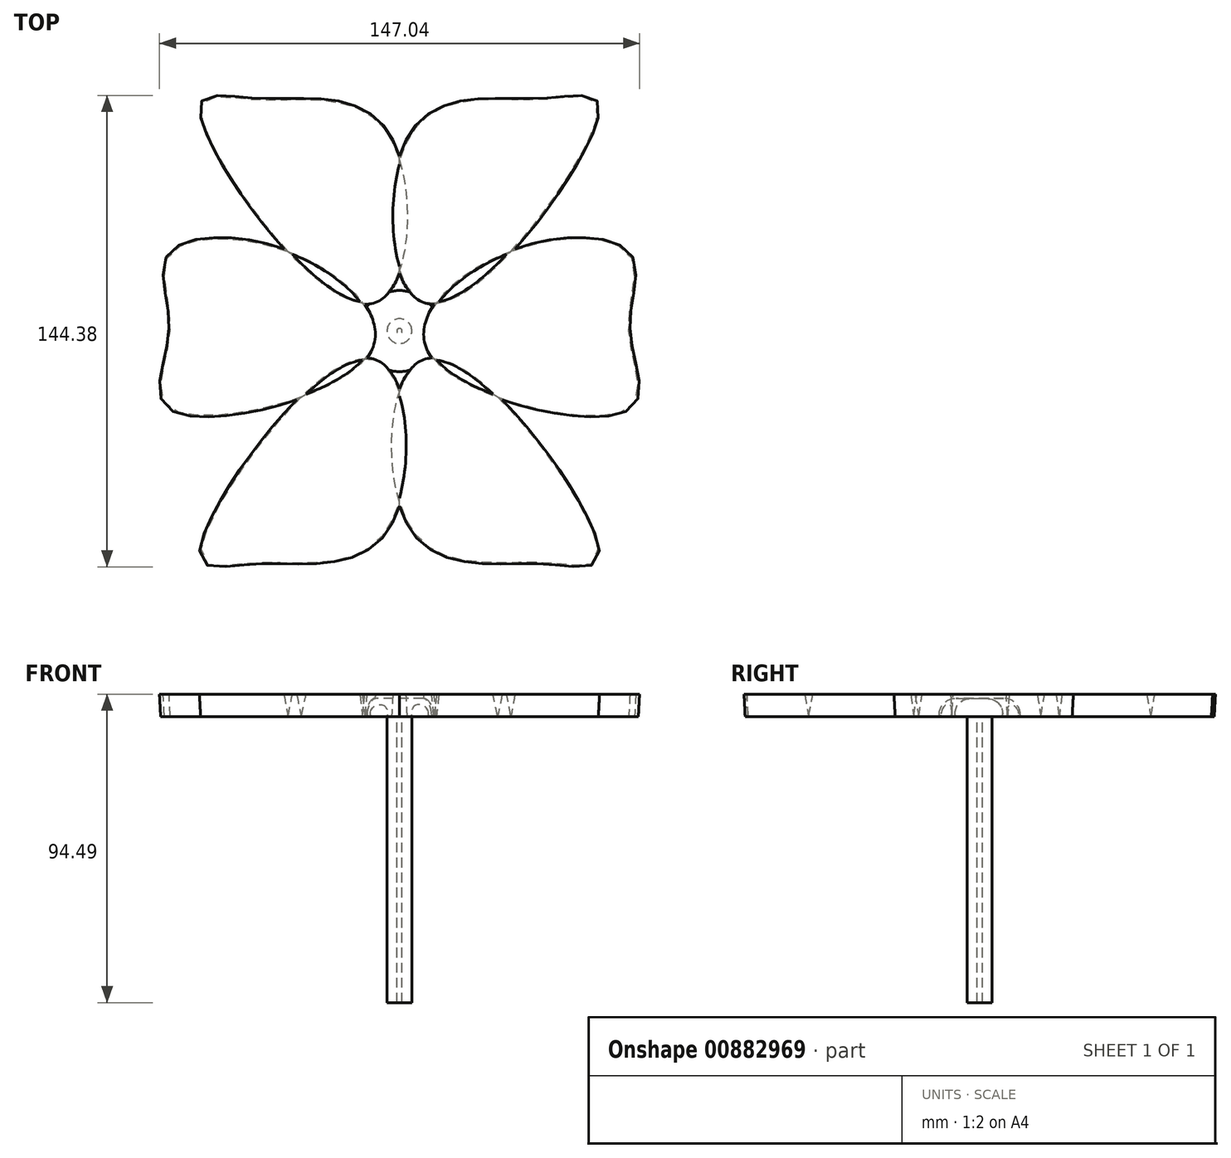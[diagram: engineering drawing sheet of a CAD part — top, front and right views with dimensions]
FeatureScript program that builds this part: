
annotation { "Feature Type Name" : "Feature", "Feature Type Description" : "" }
export const myFeature = defineFeature(function(context is Context, id is Id, definition is map)
    precondition{}
    {
        {
            var Q0;
            Q0=qCreatedBy(makeId("Top.planeOp"),FACE);
            var sketch = newSketch(context, id + "F0", { "sketchPlane" : qUnion([Q0])});
            skCircle(sketch, "E0", {"center": v(0, 0) * mm, "radius": 0.81 * mm});
            skCircle(sketch, "E1", {"center": v(0, 0) * mm, "radius": 3.8 * mm});
            skSolve(sketch);
        }
        {
            var Q0;
            Q0=makeQuery(id+"F0.imprint","IMPRINT",FACE,{"disambiguationData":[TD([[makeQuery(id+"F0.imprint","IMPRINT",EDGE,{"derivedFrom":sQuery(id+"F0.wireOp",EDGE,"E0")}),-1.0]])]});
            extrude(context, id + "F1", {"entities" : qUnion([Q0]), "oppositeDirection" : true, "depth" : 87.63 * mm, "offsetDistance" : 25.4 * mm});
        }
        {
            var Q0;
            Q0=qCreatedBy(makeId("Top.planeOp"),FACE);
            var sketch = newSketch(context, id + "F2", { "sketchPlane" : qUnion([Q0])});
            skCircle(sketch, "E2", {"center": v(0, 0) * mm, "radius": 12.41 * mm});
            skSolve(sketch);
        }
        {
            var Q0;
            Q0=makeQuery(id+"F2.imprint","IMPRINT",FACE,{"disambiguationData":[TD([[makeQuery(id+"F2.imprint","IMPRINT",EDGE,{"derivedFrom":sQuery(id+"F2.wireOp",EDGE,"E2")}),1.0]])]});
            extrude(context, id + "F3", {"entities" : qUnion([Q0]), "operationType" : NewBodyOperationType.ADD, "depth" : 5.6 * mm, "offsetDistance" : 25.4 * mm});
        }
        {
            var Q0;
            Q0=makeQuery(id+"F3.opExtrude","CAP_EDGE",EDGE,{"disambiguationData":[OSD([sQuery(id+"F2.wireOp",EDGE,"E2")])],"isStart":false});
            fillet(context, id + "F4", {"entities" : qUnion([Q0]), "radius" : 5.08 * mm, "tangentPropagation" : true, "allowEdgeOverflow" : false});
        }
        {
            var Q0;
            Q0=qCreatedBy(makeId("Top.planeOp"),FACE);
            var sketch = newSketch(context, id + "F5", { "sketchPlane" : qUnion([Q0])});
            skFitSpline(sketch, "E3", {"points": [v(9.45, 8.57) * mm, v(60.92, 68.12) * mm, v(44.56, 71) * mm, v(3.8, 60.86) * mm, v(9.45, 8.57) * mm]});
            skFitSpline(sketch, "E4", {"points": [v(70.26, -23.74) * mm, v(70.26, 0) * mm, v(70.55, 23.46) * mm, v(30.95, 23.11) * mm, v(9.61, -7.16) * mm, v(70.26, -23.74) * mm]});
            skFitSpline(sketch, "E5.MirrorC", {"points": [v(9.45, -8.57) * mm, v(60.92, -68.12) * mm, v(44.56, -71) * mm, v(3.8, -60.86) * mm, v(9.45, -8.57) * mm]});
            skFitSpline(sketch, "E6.MirrorC", {"points": [v(-9.45, 8.57) * mm, v(-60.92, 68.12) * mm, v(-44.56, 71) * mm, v(-3.8, 60.86) * mm, v(-9.45, 8.57) * mm]});
            skFitSpline(sketch, "E7.MirrorC", {"points": [v(-70.26, -23.74) * mm, v(-70.26, 0) * mm, v(-70.55, 23.46) * mm, v(-30.95, 23.11) * mm, v(-9.61, -7.16) * mm, v(-70.26, -23.74) * mm]});
            skFitSpline(sketch, "E8.MirrorC", {"points": [v(-9.45, -8.57) * mm, v(-60.92, -68.12) * mm, v(-44.56, -71) * mm, v(-3.8, -60.86) * mm, v(-9.45, -8.57) * mm]});
            skLineSegment(sketch, "E9", {"start": v(0, -8.33) * mm, "end": v(0, -126.74) * mm});
            skSolve(sketch);
        }
        {
            var Q0;
            {var subQ1=sQuery(id+"F5.wireOp",EDGE,"E8.MirrorC");var subQ5=sQuery(id+"F5.wireOp",EDGE,"E7.MirrorC");var subQ6=makeQuery(id+"F5.imprint","INTERSECT",VERTEX,{"disambiguationData":[OD(0.0)],"derivedFrom":[subQ5,subQ1]});Q0=makeQuery(id+"F5.imprint","IMPRINT",FACE,{"disambiguationData":[TD([[makeQuery(id+"F5.imprint","IMPRINT",EDGE,{"disambiguationData":[TD([[subQ6,1.0]])],"derivedFrom":subQ5}),1.0]])]});}
            var Q1;
            {var subQ0=sQuery(id+"F5.wireOp",EDGE,"E6.MirrorC");var subQ1=sQuery(id+"F5.wireOp",EDGE,"E3");var subQ2=makeQuery(id+"F5.imprint","INTERSECT",VERTEX,{"disambiguationData":[OD(0.0)],"derivedFrom":[subQ1,subQ0]});Q1=makeQuery(id+"F5.imprint","IMPRINT",FACE,{"disambiguationData":[TD([[makeQuery(id+"F5.imprint","IMPRINT",EDGE,{"disambiguationData":[TD([[subQ2,-1.0]])],"derivedFrom":subQ1}),-1.0]])]});}
            var Q2;
            {var subQ0=sQuery(id+"F5.wireOp",EDGE,"E4");var subQ1=sQuery(id+"F5.wireOp",EDGE,"E3");var subQ2=makeQuery(id+"F5.imprint","INTERSECT",VERTEX,{"disambiguationData":[OD(0.0)],"derivedFrom":[subQ1,subQ0]});Q2=makeQuery(id+"F5.imprint","IMPRINT",FACE,{"disambiguationData":[TD([[makeQuery(id+"F5.imprint","IMPRINT",EDGE,{"disambiguationData":[TD([[subQ2,-1.0]])],"derivedFrom":subQ1}),1.0]])]});}
            var Q3;
            {var subQ0=sQuery(id+"F5.wireOp",EDGE,"E4");var subQ1=sQuery(id+"F5.wireOp",EDGE,"E3");var subQ2=makeQuery(id+"F5.imprint","INTERSECT",VERTEX,{"disambiguationData":[OD(0.0)],"derivedFrom":[subQ1,subQ0]});Q3=makeQuery(id+"F5.imprint","IMPRINT",FACE,{"disambiguationData":[TD([[makeQuery(id+"F5.imprint","IMPRINT",EDGE,{"disambiguationData":[TD([[subQ2,1.0]])],"derivedFrom":subQ1}),-1.0]])]});}
            var Q4;
            {var subQ0=sQuery(id+"F5.wireOp",EDGE,"E5.MirrorC");var subQ1=sQuery(id+"F5.wireOp",EDGE,"E4");var subQ2=makeQuery(id+"F5.imprint","INTERSECT",VERTEX,{"disambiguationData":[OD(0.0)],"derivedFrom":[subQ1,subQ0]});Q4=makeQuery(id+"F5.imprint","IMPRINT",FACE,{"disambiguationData":[TD([[makeQuery(id+"F5.imprint","IMPRINT",EDGE,{"disambiguationData":[TD([[subQ2,1.0]])],"derivedFrom":subQ1}),-1.0]])]});}
            var Q5;
            {var subQ0=sQuery(id+"F5.wireOp",EDGE,"E7.MirrorC");var subQ1=sQuery(id+"F5.wireOp",EDGE,"E6.MirrorC");var subQ2=makeQuery(id+"F5.imprint","INTERSECT",VERTEX,{"disambiguationData":[OD(0.0)],"derivedFrom":[subQ1,subQ0]});Q5=makeQuery(id+"F5.imprint","IMPRINT",FACE,{"disambiguationData":[TD([[makeQuery(id+"F5.imprint","IMPRINT",EDGE,{"disambiguationData":[TD([[subQ2,1.0]])],"derivedFrom":subQ1}),1.0]])]});}
            extrude(context, id + "F6", {"entities" : qUnion([Q0, Q1, Q2, Q3, Q4, Q5]), "operationType" : NewBodyOperationType.ADD, "depth" : 6.86 * mm, "offsetDistance" : 25.4 * mm, "hasDraft" : true, "draftAngle" : 3 * degree});
        }
    });
